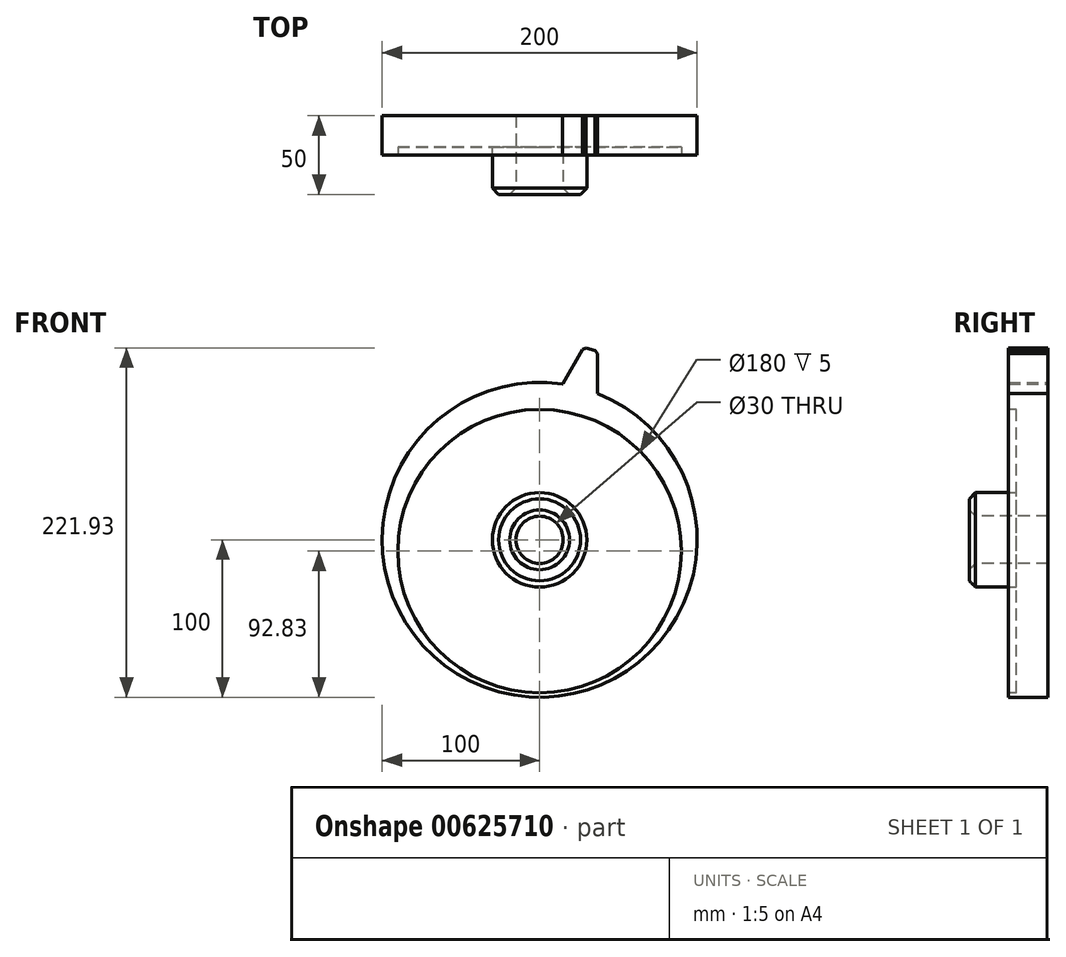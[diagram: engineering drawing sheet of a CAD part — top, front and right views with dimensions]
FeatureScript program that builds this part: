
annotation { "Feature Type Name" : "Feature", "Feature Type Description" : "" }
export const myFeature = defineFeature(function(context is Context, id is Id, definition is map)
    precondition{}
    {
        {
            var Q0;
            Q0=qCreatedBy(makeId("Front.planeOp"),FACE);
            var sketch = newSketch(context, id + "F0", { "sketchPlane" : qUnion([Q0])});
            skCircle(sketch, "E0", {"center": v(0, 0) * mm, "radius": 100 * mm});
            skSolve(sketch);
        }
        {
            var Q0;
            Q0 = qSketchRegion(id + "F0", true);
            extrude(context, id + "F1", {"entities" : qUnion([Q0]), "depth" : 25 * mm, "offsetDistance" : 25 * mm});
        }
        {
            var Q0;
            Q0=makeQuery(id+"F1.opExtrude","CAP_FACE",FACE,{"disambiguationData":[OSD([sQuery(id+"F0.wireOp",EDGE,"E0")])],"isStart":false});
            var sketch = newSketch(context, id + "F2", { "sketchPlane" : qUnion([Q0])});
            skLineSegment(sketch, "E1", {"start": v(14.6, 98.93) * mm, "end": v(28.12, 122.33) * mm});
            skLineSegment(sketch, "E2", {"start": v(28.12, 122.33) * mm, "end": v(36.81, 120) * mm});
            skLineSegment(sketch, "E3", {"start": v(36.81, 120) * mm, "end": v(36.81, 92.98) * mm});
            skLineSegment(sketch, "E4", {"start": v(36.81, 92.98) * mm, "end": v(14.6, 98.93) * mm});
            skSolve(sketch);
        }
        {
            var Q0;
            Q0 = qSketchRegion(id + "F2", true);
            extrude(context, id + "F3", {"entities" : qUnion([Q0]), "operationType" : NewBodyOperationType.ADD, "oppositeDirection" : true, "depth" : 25 * mm, "offsetDistance" : 25 * mm});
        }
        {
            var Q0;
            Q0=makeQuery(id+"F3.opExtrude","SWEPT_EDGE",EDGE,{"disambiguationData":[OSD([sQuery(id+"F0.wireOp",EDGE,"E0"),sQuery(id+"F2.wireOp",EDGE,"E1"),sQuery(id+"F2.wireOp",EDGE,"E4")])]});
            var Q1;
            Q1=makeQuery(id+"F3.opExtrude","SWEPT_EDGE",EDGE,{"disambiguationData":[OSD([sQuery(id+"F0.wireOp",EDGE,"E0"),sQuery(id+"F2.wireOp",EDGE,"E3"),sQuery(id+"F2.wireOp",EDGE,"E4")])]});
            fillet(context, id + "F4", {"entities" : qUnion([Q0, Q1]), "radius" : 5 * mm, "tangentPropagation" : true, "allowEdgeOverflow" : false});
        }
        {
            var Q0;
            Q0=makeQuery(id+"F3.opExtrude","SWEPT_EDGE",EDGE,{"disambiguationData":[OSD([sQuery(id+"F2.wireOp",EDGE,"E2"),sQuery(id+"F2.wireOp",EDGE,"E3")])]});
            var Q1;
            Q1=makeQuery(id+"F3.opExtrude","SWEPT_EDGE",EDGE,{"disambiguationData":[OSD([sQuery(id+"F2.wireOp",EDGE,"E1"),sQuery(id+"F2.wireOp",EDGE,"E2")])]});
            chamfer(context, id + "F5", {"entities" : qUnion([Q0, Q1]), "width" : 2 * mm, "tangentPropagation" : true});
        }
        {
            var Q0;
            {var subQ0=sQuery(id+"F2.wireOp",EDGE,"E4");var subQ1=sQuery(id+"F2.wireOp",EDGE,"E3");var subQ2=sQuery(id+"F2.wireOp",EDGE,"E2");var subQ3=sQuery(id+"F2.wireOp",EDGE,"E1");Q0=makeQuery(id+"FBd5aibeAN1q0wt_1.19.F3.boolean.opBoolean","MERGE",FACE,{"derivedFrom":[makeQuery(id+"FBd5aibeAN1q0wt_1.18.F3.boolean.opBoolean","MERGE",FACE,{"derivedFrom":[makeQuery(id+"FBd5aibeAN1q0wt_1.17.F3.boolean.opBoolean","MERGE",FACE,{"derivedFrom":[makeQuery(id+"FBd5aibeAN1q0wt_1.16.F3.boolean.opBoolean","MERGE",FACE,{"derivedFrom":[makeQuery(id+"FBd5aibeAN1q0wt_1.15.F3.boolean.opBoolean","MERGE",FACE,{"derivedFrom":[makeQuery(id+"FBd5aibeAN1q0wt_1.14.F3.boolean.opBoolean","MERGE",FACE,{"derivedFrom":[makeQuery(id+"FBd5aibeAN1q0wt_1.13.F3.boolean.opBoolean","MERGE",FACE,{"derivedFrom":[makeQuery(id+"FBd5aibeAN1q0wt_1.12.F3.boolean.opBoolean","MERGE",FACE,{"derivedFrom":[makeQuery(id+"FBd5aibeAN1q0wt_1.11.F3.boolean.opBoolean","MERGE",FACE,{"derivedFrom":[makeQuery(id+"FBd5aibeAN1q0wt_1.10.F3.boolean.opBoolean","MERGE",FACE,{"derivedFrom":[makeQuery(id+"FBd5aibeAN1q0wt_1.9.F3.boolean.opBoolean","MERGE",FACE,{"derivedFrom":[makeQuery(id+"FBd5aibeAN1q0wt_1.8.F3.boolean.opBoolean","MERGE",FACE,{"derivedFrom":[makeQuery(id+"FBd5aibeAN1q0wt_1.7.F3.boolean.opBoolean","MERGE",FACE,{"derivedFrom":[makeQuery(id+"FBd5aibeAN1q0wt_1.6.F3.boolean.opBoolean","MERGE",FACE,{"derivedFrom":[makeQuery(id+"FBd5aibeAN1q0wt_1.5.F3.boolean.opBoolean","MERGE",FACE,{"derivedFrom":[makeQuery(id+"FBd5aibeAN1q0wt_1.4.F3.boolean.opBoolean","MERGE",FACE,{"derivedFrom":[makeQuery(id+"FBd5aibeAN1q0wt_1.3.F3.boolean.opBoolean","MERGE",FACE,{"derivedFrom":[makeQuery(id+"FBd5aibeAN1q0wt_1.2.F3.boolean.opBoolean","MERGE",FACE,{"derivedFrom":[makeQuery(id+"FBd5aibeAN1q0wt_1.1.F3.boolean.opBoolean","MERGE",FACE,{"derivedFrom":[makeQuery(id+"F3.boolean.opBoolean","MERGE",FACE,{"derivedFrom":[makeQuery(id+"F1.opExtrude","CAP_FACE",FACE,{"disambiguationData":[OSD([sQuery(id+"F0.wireOp",EDGE,"E0")])],"isStart":false}),makeQuery(id+"F3.opExtrude","CAP_FACE",FACE,{"disambiguationData":[OSD([subQ3,subQ2,subQ1,subQ0])],"isStart":true})]}),makeQuery(id+"FBd5aibeAN1q0wt_1.1.F3.opExtrude","CAP_FACE",FACE,{"disambiguationData":[OSD([subQ3,subQ2,subQ1,subQ0])],"isStart":true})]}),makeQuery(id+"FBd5aibeAN1q0wt_1.2.F3.opExtrude","CAP_FACE",FACE,{"disambiguationData":[OSD([subQ3,subQ2,subQ1,subQ0])],"isStart":true})]}),makeQuery(id+"FBd5aibeAN1q0wt_1.3.F3.opExtrude","CAP_FACE",FACE,{"disambiguationData":[OSD([subQ3,subQ2,subQ1,subQ0])],"isStart":true})]}),makeQuery(id+"FBd5aibeAN1q0wt_1.4.F3.opExtrude","CAP_FACE",FACE,{"disambiguationData":[OSD([subQ3,subQ2,subQ1,subQ0])],"isStart":true})]}),makeQuery(id+"FBd5aibeAN1q0wt_1.5.F3.opExtrude","CAP_FACE",FACE,{"disambiguationData":[OSD([subQ3,subQ2,subQ1,subQ0])],"isStart":true})]}),makeQuery(id+"FBd5aibeAN1q0wt_1.6.F3.opExtrude","CAP_FACE",FACE,{"disambiguationData":[OSD([subQ3,subQ2,subQ1,subQ0])],"isStart":true})]}),makeQuery(id+"FBd5aibeAN1q0wt_1.7.F3.opExtrude","CAP_FACE",FACE,{"disambiguationData":[OSD([subQ3,subQ2,subQ1,subQ0])],"isStart":true})]}),makeQuery(id+"FBd5aibeAN1q0wt_1.8.F3.opExtrude","CAP_FACE",FACE,{"disambiguationData":[OSD([subQ3,subQ2,subQ1,subQ0])],"isStart":true})]}),makeQuery(id+"FBd5aibeAN1q0wt_1.9.F3.opExtrude","CAP_FACE",FACE,{"disambiguationData":[OSD([subQ3,subQ2,subQ1,subQ0])],"isStart":true})]}),makeQuery(id+"FBd5aibeAN1q0wt_1.10.F3.opExtrude","CAP_FACE",FACE,{"disambiguationData":[OSD([subQ3,subQ2,subQ1,subQ0])],"isStart":true})]}),makeQuery(id+"FBd5aibeAN1q0wt_1.11.F3.opExtrude","CAP_FACE",FACE,{"disambiguationData":[OSD([subQ3,subQ2,subQ1,subQ0])],"isStart":true})]}),makeQuery(id+"FBd5aibeAN1q0wt_1.12.F3.opExtrude","CAP_FACE",FACE,{"disambiguationData":[OSD([subQ3,subQ2,subQ1,subQ0])],"isStart":true})]}),makeQuery(id+"FBd5aibeAN1q0wt_1.13.F3.opExtrude","CAP_FACE",FACE,{"disambiguationData":[OSD([subQ3,subQ2,subQ1,subQ0])],"isStart":true})]}),makeQuery(id+"FBd5aibeAN1q0wt_1.14.F3.opExtrude","CAP_FACE",FACE,{"disambiguationData":[OSD([subQ3,subQ2,subQ1,subQ0])],"isStart":true})]}),makeQuery(id+"FBd5aibeAN1q0wt_1.15.F3.opExtrude","CAP_FACE",FACE,{"disambiguationData":[OSD([subQ3,subQ2,subQ1,subQ0])],"isStart":true})]}),makeQuery(id+"FBd5aibeAN1q0wt_1.16.F3.opExtrude","CAP_FACE",FACE,{"disambiguationData":[OSD([subQ3,subQ2,subQ1,subQ0])],"isStart":true})]}),makeQuery(id+"FBd5aibeAN1q0wt_1.17.F3.opExtrude","CAP_FACE",FACE,{"disambiguationData":[OSD([subQ3,subQ2,subQ1,subQ0])],"isStart":true})]}),makeQuery(id+"FBd5aibeAN1q0wt_1.18.F3.opExtrude","CAP_FACE",FACE,{"disambiguationData":[OSD([subQ3,subQ2,subQ1,subQ0])],"isStart":true})]}),makeQuery(id+"FBd5aibeAN1q0wt_1.19.F3.opExtrude","CAP_FACE",FACE,{"disambiguationData":[OSD([subQ3,subQ2,subQ1,subQ0])],"isStart":true})]});}
            var sketch = newSketch(context, id + "F6", { "sketchPlane" : qUnion([Q0])});
            skCircle(sketch, "E5", {"center": v(0, -7.17) * mm, "radius": 90 * mm});
            skSolve(sketch);
        }
        {
            var Q0;
            Q0 = qSketchRegion(id + "F6", true);
            extrude(context, id + "F7", {"entities" : qUnion([Q0]), "operationType" : NewBodyOperationType.REMOVE, "oppositeDirection" : true, "depth" : 5 * mm, "offsetDistance" : 25 * mm});
        }
        {
            var Q0;
            Q0=makeQuery(id+"F7.boolean.opBoolean","COPY",FACE,{"derivedFrom":makeQuery(id+"F7.opExtrude","CAP_FACE",FACE,{"disambiguationData":[OSD([sQuery(id+"F6.wireOp",EDGE,"E5")])],"isStart":false})});
            var sketch = newSketch(context, id + "F8", { "sketchPlane" : qUnion([Q0])});
            skCircle(sketch, "E6", {"center": v(0, 0) * mm, "radius": 30 * mm});
            skSolve(sketch);
        }
        {
            var Q0;
            Q0=makeQuery(id+"F8.imprint","IMPRINT",FACE,{"disambiguationData":[TD([[makeQuery(id+"F8.imprint","IMPRINT",EDGE,{"derivedFrom":sQuery(id+"F8.wireOp",EDGE,"E6")}),1.0]])]});
            extrude(context, id + "F9", {"entities" : qUnion([Q0]), "operationType" : NewBodyOperationType.ADD, "depth" : 30 * mm, "offsetDistance" : 25 * mm});
        }
        {
            var Q0;
            Q0=makeQuery(id+"F9.opExtrude","CAP_FACE",FACE,{"disambiguationData":[OSD([sQuery(id+"F8.wireOp",EDGE,"E6")])],"isStart":false});
            var sketch = newSketch(context, id + "F10", { "sketchPlane" : qUnion([Q0])});
            skCircle(sketch, "E7", {"center": v(0, 0) * mm, "radius": 15 * mm});
            skSolve(sketch);
        }
        {
            var Q0;
            Q0=makeQuery(id+"F10.imprint","IMPRINT",FACE,{"disambiguationData":[TD([[makeQuery(id+"F10.imprint","IMPRINT",EDGE,{"derivedFrom":sQuery(id+"F10.wireOp",EDGE,"E7")}),1.0]])]});
            extrude(context, id + "F11", {"entities" : qUnion([Q0]), "operationType" : NewBodyOperationType.REMOVE, "endBound" : BoundingType.THROUGH_ALL, "oppositeDirection" : true, "depth" : 25 * mm, "offsetDistance" : 25 * mm});
        }
        {
            var Q0;
            Q0=makeQuery(id+"F9.opExtrude","CAP_FACE",FACE,{"disambiguationData":[OSD([sQuery(id+"F8.wireOp",EDGE,"E6")])],"isStart":false});
            chamfer(context, id + "F12", {"entities" : qUnion([Q0]), "width" : 4 * mm, "tangentPropagation" : true});
        }
    });
